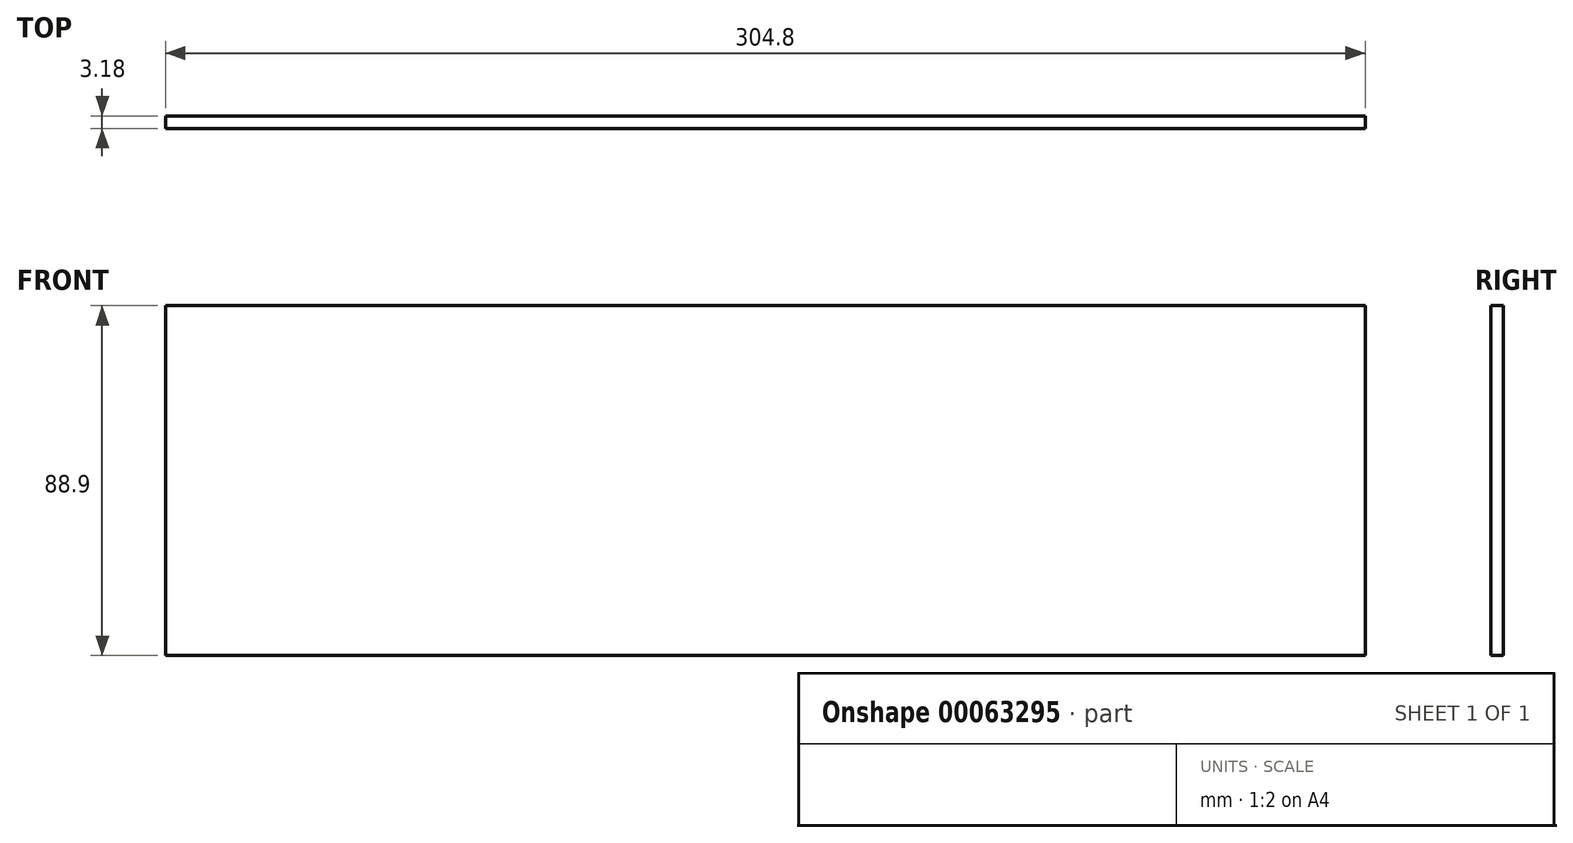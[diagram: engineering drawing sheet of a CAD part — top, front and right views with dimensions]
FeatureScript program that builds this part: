
annotation { "Feature Type Name" : "Feature", "Feature Type Description" : "" }
export const myFeature = defineFeature(function(context is Context, id is Id, definition is map)
    precondition{}
    {
        {
            var Q0;
            Q0=qCreatedBy(makeId("Front.planeOp"),FACE);
            var sketch = newSketch(context, id + "F0", { "sketchPlane" : qUnion([Q0])});
            skLineSegment(sketch, "E0.rect.bottom", {"start": v(152.4, 34.33) * mm, "end": v(-152.4, 34.33) * mm});
            skLineSegment(sketch, "E0.rect.top", {"start": v(152.4, -54.57) * mm, "end": v(-152.4, -54.57) * mm});
            skLineSegment(sketch, "E0.rect.left", {"start": v(152.4, 34.33) * mm, "end": v(152.4, -54.57) * mm});
            skLineSegment(sketch, "E0.rect.right", {"start": v(-152.4, 34.33) * mm, "end": v(-152.4, -54.57) * mm});
            skPoint(sketch, "E0.rect.middle", {"position": v(0, -10.12) * mm});
            skSolve(sketch);
        }
        {
            var Q0;
            Q0=makeQuery(id+"F0.imprint","IMPRINT",FACE,{"disambiguationData":[TD([[makeQuery(id+"F0.imprint","IMPRINT",EDGE,{"derivedFrom":sQuery(id+"F0.wireOp",EDGE,"E0.rect.bottom")}),1.0]])]});
            extrude(context, id + "F1", {"entities" : qUnion([Q0]), "depth" : 3.17 * mm, "symmetric" : true});
        }
    });
